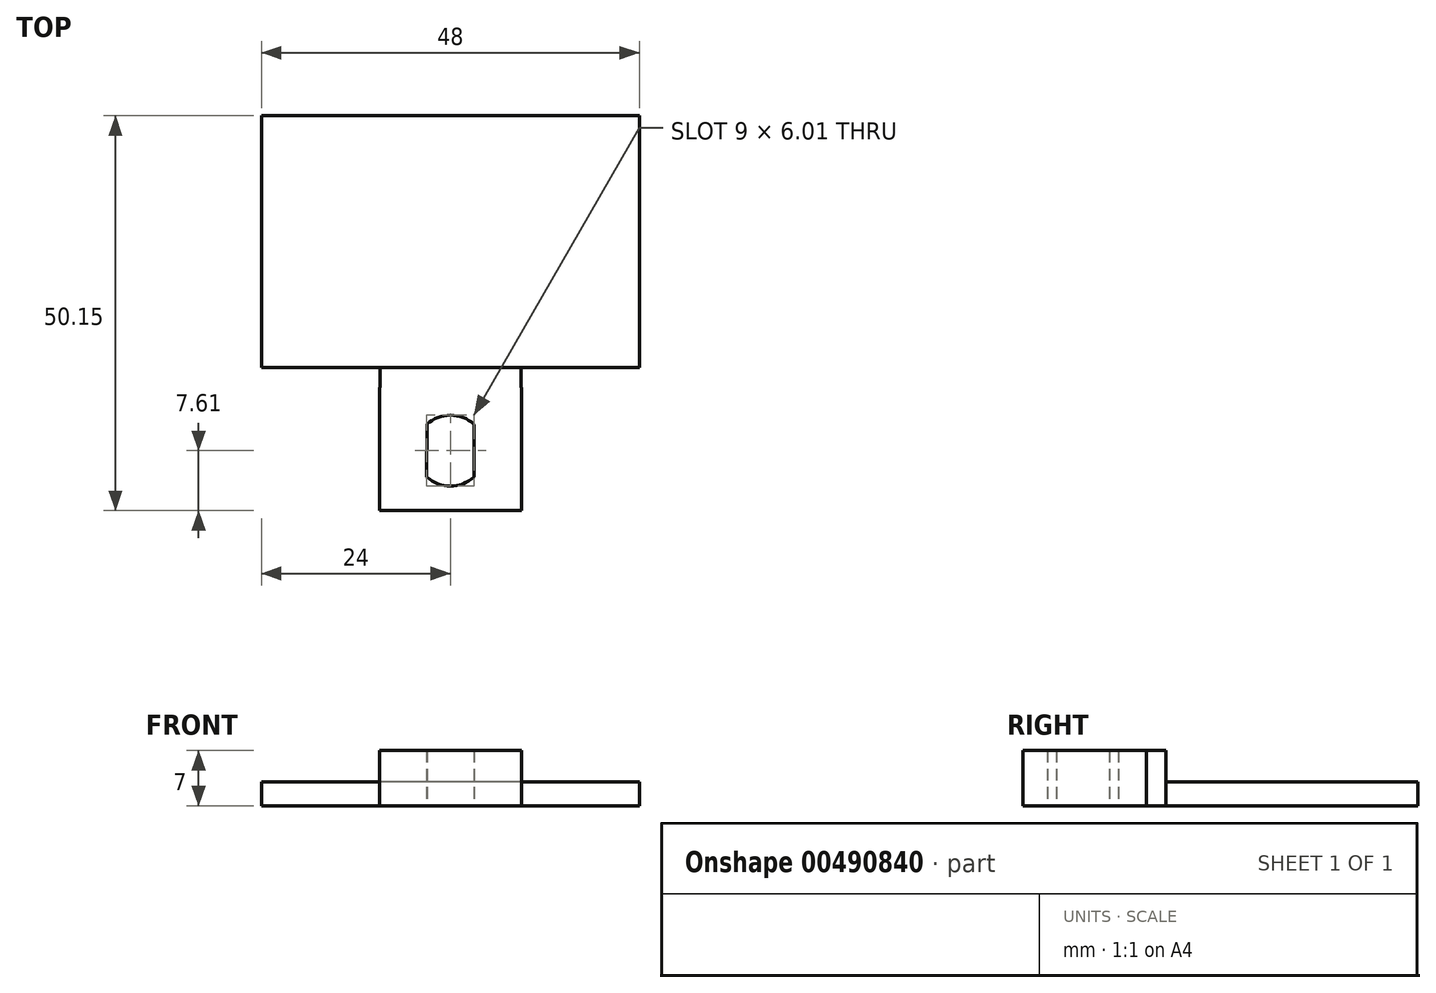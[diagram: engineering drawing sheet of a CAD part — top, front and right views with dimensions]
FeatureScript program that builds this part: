
annotation { "Feature Type Name" : "Feature", "Feature Type Description" : "" }
export const myFeature = defineFeature(function(context is Context, id is Id, definition is map)
    precondition{}
    {
        {
            var Q0;
            Q0=qCreatedBy(makeId("Top.planeOp"),FACE);
            var sketch = newSketch(context, id + "F0", { "sketchPlane" : qUnion([Q0])});
            skLineSegment(sketch, "E0", {"start": v(-6.36, 8.04) * mm, "end": v(0, 8.04) * mm});
            skLineSegment(sketch, "E1", {"start": v(0, 8.04) * mm, "end": v(6.36, 8.04) * mm});
            skLineSegment(sketch, "E2.bottom", {"start": v(9, 8.04) * mm, "end": v(-9, 8.04) * mm});
            skLineSegment(sketch, "E2.top", {"start": v(9, -7.6) * mm, "end": v(-9, -7.6) * mm});
            skLineSegment(sketch, "E2.left", {"start": v(9, 8.04) * mm, "end": v(9, -7.6) * mm});
            skLineSegment(sketch, "E2.right", {"start": v(-9, 8.04) * mm, "end": v(-9, -7.6) * mm});
            skPoint(sketch, "E2.middle", {"position": v(0, 0.21) * mm});
            skLineSegment(sketch, "E3.left", {"start": v(3, -3.36) * mm, "end": v(3, 3.35) * mm});
            skLineSegment(sketch, "E3.right", {"start": v(-3, -3.35) * mm, "end": v(-3, 3.36) * mm});
            skLineSegment(sketch, "E4.bottom", {"start": v(-9, 8.04) * mm, "end": v(-6.36, 8.04) * mm});
            skLineSegment(sketch, "E4.left", {"start": v(-9, 8.04) * mm, "end": v(-9, 8.04) * mm});
            skLineSegment(sketch, "E4.right", {"start": v(9, 8.04) * mm, "end": v(9, 8.04) * mm});
            skPoint(sketch, "E5.middle", {"position": v(0, 12.27) * mm});
            skLineSegment(sketch, "E6", {"start": v(-8.96, 8.04) * mm, "end": v(-8.96, 10.54) * mm});
            skLineSegment(sketch, "E7", {"start": v(-8.96, 10.54) * mm, "end": v(0, 10.54) * mm});
            skLineSegment(sketch, "E8.MirrorCS", {"start": v(8.96, 8.04) * mm, "end": v(8.96, 10.54) * mm});
            skLineSegment(sketch, "E9.MirrorCS", {"start": v(8.96, 10.54) * mm, "end": v(0, 10.54) * mm});
            skLineSegment(sketch, "E10", {"start": v(8.96, 10.54) * mm, "end": v(24, 10.54) * mm});
            skLineSegment(sketch, "E11", {"start": v(24, 10.54) * mm, "end": v(24, 15.54) * mm});
            skLineSegment(sketch, "E12", {"start": v(24, 15.54) * mm, "end": v(0, 15.54) * mm});
            skLineSegment(sketch, "E13.MirrorCS", {"start": v(-8.96, 10.54) * mm, "end": v(-24, 10.54) * mm});
            skLineSegment(sketch, "E14.MirrorCS", {"start": v(-24, 15.54) * mm, "end": v(0, 15.54) * mm});
            skLineSegment(sketch, "E15.MirrorCS", {"start": v(-24, 10.54) * mm, "end": v(-24, 15.54) * mm});
            skArc(sketch, "E16", {"start": v(3, 3.35) * mm, "mid": v(0, 4.5) * mm, "end": v(-3, 3.36) * mm});
            skPoint(sketch, "E17.orphan", {"position": v(3, 3.63) * mm});
            skArc(sketch, "E18.trimOffspring", {"start": v(-3, -3.35) * mm, "mid": v(0, -4.5) * mm, "end": v(3, -3.36) * mm});
            skPoint(sketch, "E19.orphan", {"position": v(-3, 4.42) * mm});
            skPoint(sketch, "E20.orphan", {"position": v(-3, -3.2) * mm});
            skPoint(sketch, "E21.orphan", {"position": v(3, -4) * mm});
            skLineSegment(sketch, "E22.trimOffspring", {"start": v(0, 8.04) * mm, "end": v(9, 8.04) * mm});
            skLineSegment(sketch, "E23.trimOffspring", {"start": v(6.36, 8.04) * mm, "end": v(9, 8.04) * mm});
            skSolve(sketch);
        }
        {
            var Q0;
            Q0=makeQuery(id+"F0.imprint","IMPRINT",FACE,{"disambiguationData":[TD([[makeQuery(id+"F0.imprint","IMPRINT",EDGE,{"derivedFrom":sQuery(id+"F0.wireOp",EDGE,"E2.top")}),-1.0]])]});
            var Q1;
            {var subQ3=sQuery(id+"F0.wireOp",EDGE,"E2.bottom");Q1=makeQuery(id+"F0.imprint","IMPRINT",FACE,{"disambiguationData":[TD([[makeQuery(id+"F0.imprint","IMPRINT",EDGE,{"derivedFrom":subQ3}),-1.0]])]});}
            extrude(context, id + "F1", {"entities" : qUnion([Q0, Q1]), "depth" : 7 * mm, "offsetDistance" : 25 * mm});
        }
        {
            var Q0;
            Q0=makeQuery(id+"F0.imprint","IMPRINT",FACE,{"disambiguationData":[TD([[makeQuery(id+"F0.imprint","IMPRINT",EDGE,{"derivedFrom":sQuery(id+"F0.wireOp",EDGE,"E7")}),1.0]])]});
            extrude(context, id + "F2", {"entities" : qUnion([Q0]), "operationType" : NewBodyOperationType.ADD, "depth" : 3 * mm, "offsetDistance" : 25 * mm});
        }
        {
            var Q0;
            Q0=makeQuery(id+"F2.opExtrude","SWEPT_FACE",FACE,{"disambiguationData":[OSD([sQuery(id+"F0.wireOp",EDGE,"E12"),sQuery(id+"F0.wireOp",EDGE,"E14.MirrorCS")])]});
            var sketch = newSketch(context, id + "F3", { "sketchPlane" : qUnion([Q0])});
            skLineSegment(sketch, "E24.bottom", {"start": v(24, 0) * mm, "end": v(-24, 0) * mm});
            skLineSegment(sketch, "E24.top", {"start": v(24, 3) * mm, "end": v(-24, 3) * mm});
            skLineSegment(sketch, "E24.left", {"start": v(24, 0) * mm, "end": v(24, 3) * mm});
            skLineSegment(sketch, "E24.right", {"start": v(-24, 0) * mm, "end": v(-24, 3) * mm});
            skSolve(sketch);
        }
        {
            var Q0;
            Q0=makeQuery(id+"F3.imprint","IMPRINT",FACE,{"disambiguationData":[TD([[makeQuery(id+"F3.imprint","IMPRINT",EDGE,{"derivedFrom":sQuery(id+"F3.wireOp",EDGE,"E24.bottom")}),1.0]])]});
            extrude(context, id + "F4", {"entities" : qUnion([Q0]), "operationType" : NewBodyOperationType.ADD, "depth" : 27 * mm, "offsetDistance" : 25 * mm});
        }
    });
